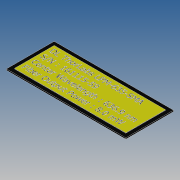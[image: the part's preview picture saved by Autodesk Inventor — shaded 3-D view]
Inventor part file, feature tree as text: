
AUTODESK INVENTOR PART (.ipt)
format: ipt  version: 2019 (Build 230136000, 136)  size: 1,835,008 bytes
history: native  units: mm
features: extrude x3, sketch x3, projected_geometry x2
ambient origin geometry x8: Origin, YZ Plane, XZ Plane, XY Plane, X Axis, Y Axis, Z Axis, Center Point
bodies: Solid1 (feature_tree)
feature tree (8):
  extrude  "Extrusion1"  Depth=12.0mm
  extrude  "Extrusion4"  Depth=0.1mm TaperAngle=0.0deg
  extrude  "Extrusion3"  Depth=1.0mm
  sketch  "Sketch1"  dims[d0=30.0mm d1=12.0mm]
  sketch  "Sketch2"  dims[d2=0.4mm d3=0.0mm d8=0.1mm d9=0.0mm]
  sketch  "Sketch3"  dims[d10=1.0mm d11=1.0mm d12=1.0mm d13=1.0mm d14=0.1mm d15=0.0mm]
  projected_geometry  "Project Cut Edges1"
  projected_geometry  "Project Cut Edges2"
